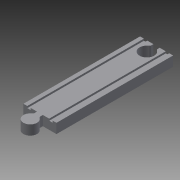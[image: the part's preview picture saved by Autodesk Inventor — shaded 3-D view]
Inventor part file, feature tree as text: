
AUTODESK INVENTOR PART (.ipt)
format: ipt  version: 2015 (Build 190159000, 159)  size: 125,440 bytes
history: native  units: in
note: dims shown in document units (in); Inventor stores cm internally (conversion verified against a paired STEP export)
features: extrude x2, sketch x2, fillet x1
ambient origin geometry x8: Origin, YZ Plane, XZ Plane, XY Plane, X Axis, Y Axis, Z Axis, Center Point
bodies: Solid1 (feature_tree)
feature tree (5):
  extrude  "Extrusion1"  Depth=0.75in
  extrude  "Extrusion2"  Depth=1.0in
  fillet  "Fillet1"  Radius=1.0in
  sketch  "Sketch1"  dims[d0=3.4in d1=0.75in]
  sketch  "Sketch2"  dims[d2=0.7in d3=1.0in d4=1.0in d5=12.0in d6=12.0in d7=0.0in d8=1.375in d9=2.025in d10=1.7in d13=1.7in d16=0.6in d17=0.3in d18=1.0in d19=0.0in d21=0.4in d22=0.75in d23=2.65in d24=3.0in d25=0.1875in d26=0.0in d27=0.19in]
